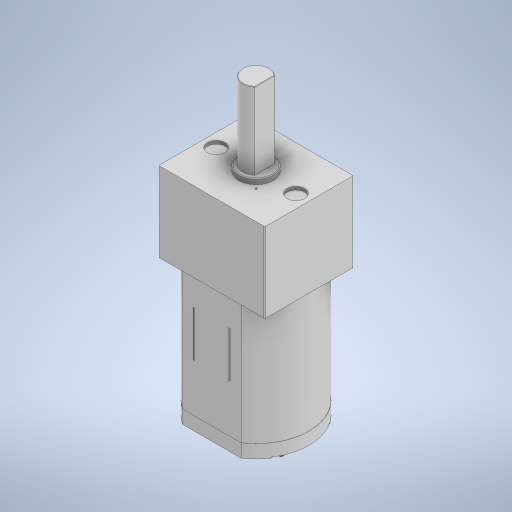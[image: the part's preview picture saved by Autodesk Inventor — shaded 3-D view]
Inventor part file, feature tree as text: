
AUTODESK INVENTOR PART (.ipt)
format: ipt  version: 2023 (Build 270158000, 158)  size: 313,856 bytes
history: native  units: in
note: dims shown in document units (in); Inventor stores cm internally (conversion verified against a paired STEP export)
features: other x2, sketch x1
ambient origin geometry x8: Origin, YZ Plane, XZ Plane, XY Plane, X Axis, Y Axis, Z Axis, Center Point
bodies: Solid1 (feature_tree), Solid2 (feature_tree)
feature tree (3):
  other  "Ñêðóãëåíèå3"
  sketch  "Sketch1"
  other  "Ñêðóãëåíèå5"
